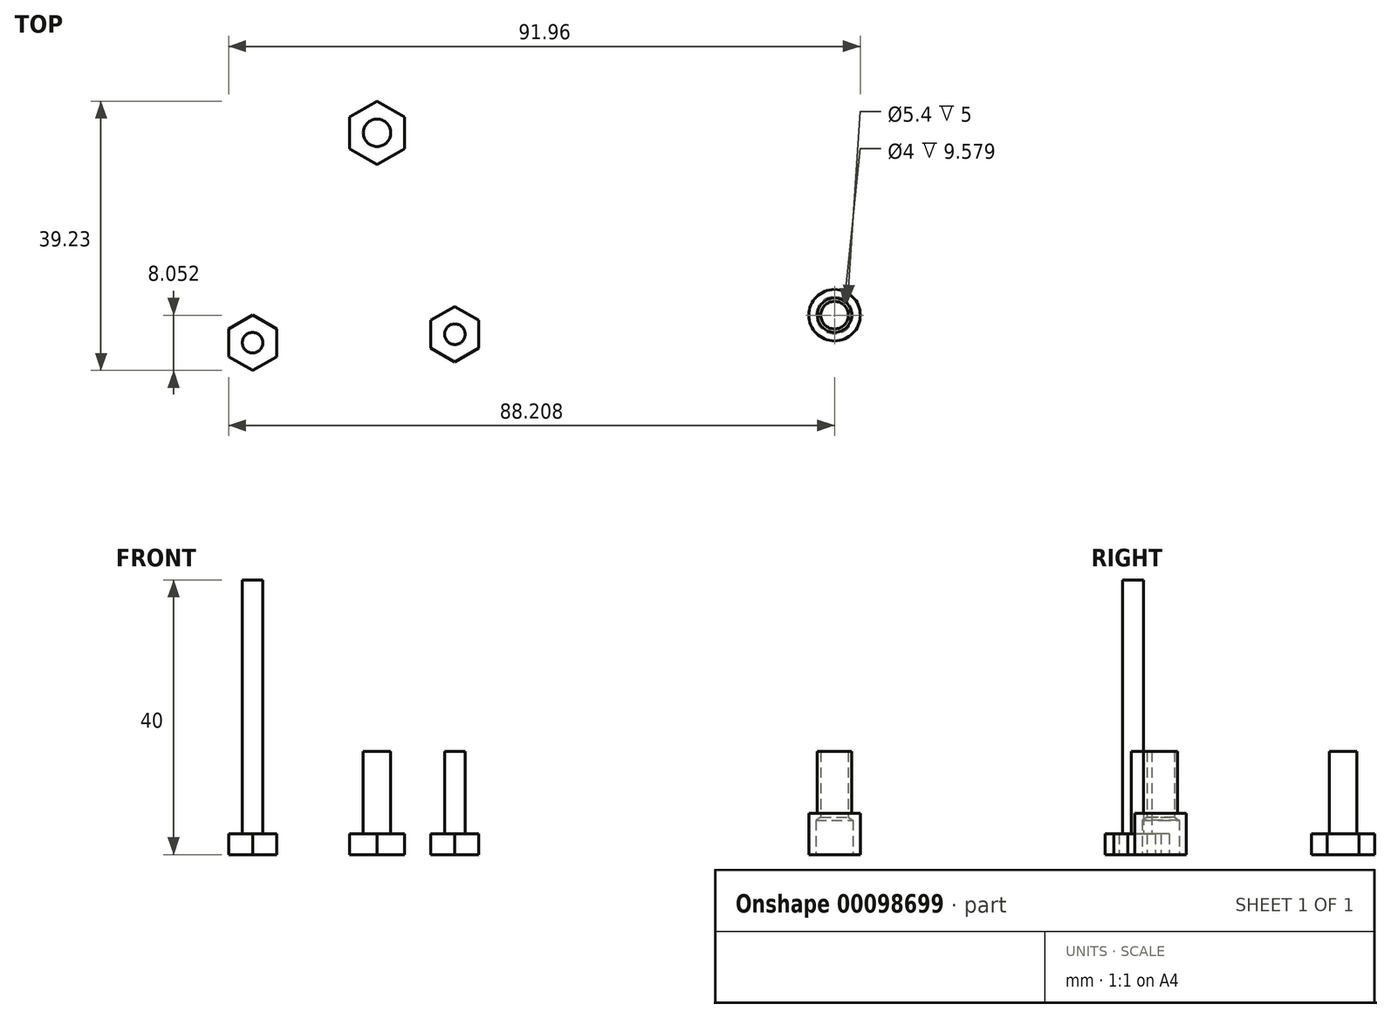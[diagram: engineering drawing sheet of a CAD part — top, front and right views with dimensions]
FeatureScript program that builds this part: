
annotation { "Feature Type Name" : "Feature", "Feature Type Description" : "" }
export const myFeature = defineFeature(function(context is Context, id is Id, definition is map)
    precondition{}
    {
        {
            var Q0;
            Q0=qCreatedBy(makeId("Top.planeOp"),FACE);
            var sketch = newSketch(context, id + "F0", { "sketchPlane" : qUnion([Q0])});
            skCircle(sketch, "E0.cCircle", {"center": v(-59.8, -54.92) * mm, "radius": 3.5 * mm, "construction": true});
            skLineSegment(sketch, "E0.0", {"start": v(-56.3, -52.9) * mm, "end": v(-56.3, -56.94) * mm});
            skLineSegment(sketch, "E0.1", {"start": v(-56.3, -56.94) * mm, "end": v(-59.8, -58.96) * mm});
            skLineSegment(sketch, "E0.2", {"start": v(-59.8, -58.96) * mm, "end": v(-63.3, -56.94) * mm});
            skLineSegment(sketch, "E0.3", {"start": v(-63.3, -56.94) * mm, "end": v(-63.3, -52.9) * mm});
            skLineSegment(sketch, "E0.4", {"start": v(-63.3, -52.9) * mm, "end": v(-59.8, -50.88) * mm});
            skLineSegment(sketch, "E0.5", {"start": v(-59.8, -50.88) * mm, "end": v(-56.3, -52.9) * mm});
            skPoint(sketch, "E0.0.midPoint", {"position": v(-56.3, -54.92) * mm});
            skCircle(sketch, "E1", {"center": v(-59.8, -54.92) * mm, "radius": 1.5 * mm});
            skCircle(sketch, "E2.cCircle", {"center": v(-30.36, -53.68) * mm, "radius": 3.5 * mm, "construction": true});
            skLineSegment(sketch, "E2.0", {"start": v(-26.86, -51.66) * mm, "end": v(-26.86, -55.7) * mm});
            skLineSegment(sketch, "E2.1", {"start": v(-26.86, -55.7) * mm, "end": v(-30.36, -57.72) * mm});
            skLineSegment(sketch, "E2.2", {"start": v(-30.36, -57.72) * mm, "end": v(-33.86, -55.7) * mm});
            skLineSegment(sketch, "E2.3", {"start": v(-33.86, -55.7) * mm, "end": v(-33.86, -51.66) * mm});
            skLineSegment(sketch, "E2.4", {"start": v(-33.86, -51.66) * mm, "end": v(-30.36, -49.64) * mm});
            skLineSegment(sketch, "E2.5", {"start": v(-30.36, -49.64) * mm, "end": v(-26.86, -51.66) * mm});
            skCircle(sketch, "E3", {"center": v(-30.36, -53.68) * mm, "radius": 1.5 * mm});
            skCircle(sketch, "E4.cCircle", {"center": v(-41.69, -24.35) * mm, "radius": 4 * mm, "construction": true});
            skLineSegment(sketch, "E4.0", {"start": v(-37.69, -22.04) * mm, "end": v(-37.69, -26.66) * mm});
            skLineSegment(sketch, "E4.1", {"start": v(-37.69, -26.66) * mm, "end": v(-41.69, -28.97) * mm});
            skLineSegment(sketch, "E4.2", {"start": v(-41.69, -28.97) * mm, "end": v(-45.69, -26.66) * mm});
            skLineSegment(sketch, "E4.3", {"start": v(-45.69, -26.66) * mm, "end": v(-45.69, -22.04) * mm});
            skLineSegment(sketch, "E4.4", {"start": v(-45.69, -22.04) * mm, "end": v(-41.69, -19.73) * mm});
            skLineSegment(sketch, "E4.5", {"start": v(-41.69, -19.73) * mm, "end": v(-37.69, -22.04) * mm});
            skCircle(sketch, "E5", {"center": v(-41.69, -24.35) * mm, "radius": 2 * mm});
            skSolve(sketch);
        }
        {
            var Q0;
            Q0=makeQuery(id+"F0.imprint","IMPRINT",FACE,{"disambiguationData":[TD([[makeQuery(id+"F0.imprint","IMPRINT",EDGE,{"derivedFrom":sQuery(id+"F0.wireOp",EDGE,"E0.0")}),-1.0]])]});
            var Q1;
            Q1=makeQuery(id+"F0.imprint","IMPRINT",FACE,{"disambiguationData":[TD([[makeQuery(id+"F0.imprint","IMPRINT",EDGE,{"derivedFrom":sQuery(id+"F0.wireOp",EDGE,"E2.0")}),-1.0]])]});
            var Q2;
            Q2=makeQuery(id+"F0.imprint","IMPRINT",FACE,{"disambiguationData":[TD([[makeQuery(id+"F0.imprint","IMPRINT",EDGE,{"derivedFrom":sQuery(id+"F0.wireOp",EDGE,"E4.0")}),-1.0]])]});
            extrude(context, id + "F1", {"entities" : qUnion([Q0, Q1, Q2]), "depth" : 3 * mm});
        }
        {
            var Q0;
            Q0=makeQuery(id+"F0.imprint","IMPRINT",FACE,{"disambiguationData":[TD([[makeQuery(id+"F0.imprint","IMPRINT",EDGE,{"derivedFrom":sQuery(id+"F0.wireOp",EDGE,"E1")}),1.0]])]});
            extrude(context, id + "F2", {"entities" : qUnion([Q0]), "operationType" : NewBodyOperationType.ADD, "depth" : 40 * mm});
        }
        {
            var Q0;
            Q0=makeQuery(id+"F0.imprint","IMPRINT",FACE,{"disambiguationData":[TD([[makeQuery(id+"F0.imprint","IMPRINT",EDGE,{"derivedFrom":sQuery(id+"F0.wireOp",EDGE,"E3")}),1.0]])]});
            var Q1;
            Q1=makeQuery(id+"F0.imprint","IMPRINT",FACE,{"disambiguationData":[TD([[makeQuery(id+"F0.imprint","IMPRINT",EDGE,{"derivedFrom":sQuery(id+"F0.wireOp",EDGE,"E5")}),1.0]])]});
            extrude(context, id + "F3", {"entities" : qUnion([Q0, Q1]), "operationType" : NewBodyOperationType.ADD, "depth" : 15 * mm});
        }
        {
            var Q0;
            Q0=qCreatedBy(makeId("Top.planeOp"),FACE);
            var sketch = newSketch(context, id + "F4", { "sketchPlane" : qUnion([Q0])});
            skCircle(sketch, "E6", {"center": v(24.9, -50.9) * mm, "radius": 3.75 * mm});
            skCircle(sketch, "E7", {"center": v(24.9, -50.9) * mm, "radius": 2.5 * mm});
            skSolve(sketch);
        }
        {
            var Q0;
            Q0=makeQuery(id+"F4.imprint","IMPRINT",FACE,{"disambiguationData":[TD([[makeQuery(id+"F4.imprint","IMPRINT",EDGE,{"derivedFrom":sQuery(id+"F4.wireOp",EDGE,"E6")}),1.0]])]});
            extrude(context, id + "F5", {"entities" : qUnion([Q0]), "depth" : 6 * mm});
        }
        {
            var Q0;
            Q0=makeQuery(id+"F4.imprint","IMPRINT",FACE,{"disambiguationData":[TD([[makeQuery(id+"F4.imprint","IMPRINT",EDGE,{"derivedFrom":sQuery(id+"F4.wireOp",EDGE,"E7")}),1.0]])]});
            extrude(context, id + "F6", {"entities" : qUnion([Q0]), "operationType" : NewBodyOperationType.ADD, "depth" : 15 * mm});
        }
        {
            var Q0;
            Q0=sQuery(id+"F4.wireOp",VERTEX,"E6.center");
            var Q1;
            Q1=makeQuery(id+"F5.opExtrude","SWEPT_BODY",BODY,{"disambiguationData":[OSD([sQuery(id+"F4.wireOp",EDGE,"E6"),sQuery(id+"F4.wireOp",EDGE,"E7")])]});
            hole(context, id + "F7", {"style" : HoleStyle.SIMPLE, "endStyle" : HoleEndStyle.BLIND, "oppositeDirection" : true, "holeDiameter" : 5.4 * mm, "holeDepth" : 5 * mm, "locations" : qUnion([Q0]), "scope" : qUnion([Q1])});
        }
        {
            var Q0;
            Q0=sQuery(id+"F4.wireOp",VERTEX,"E6.center");
            var Q1;
            Q1=makeQuery(id+"F5.opExtrude","SWEPT_BODY",BODY,{"disambiguationData":[OSD([sQuery(id+"F4.wireOp",EDGE,"E6"),sQuery(id+"F4.wireOp",EDGE,"E7")])]});
            hole(context, id + "F8", {"style" : HoleStyle.SIMPLE, "endStyle" : HoleEndStyle.BLIND, "oppositeDirection" : true, "holeDiameter" : 4 * mm, "holeDepth" : 15 * mm, "locations" : qUnion([Q0]), "scope" : qUnion([Q1])});
        }
    });
